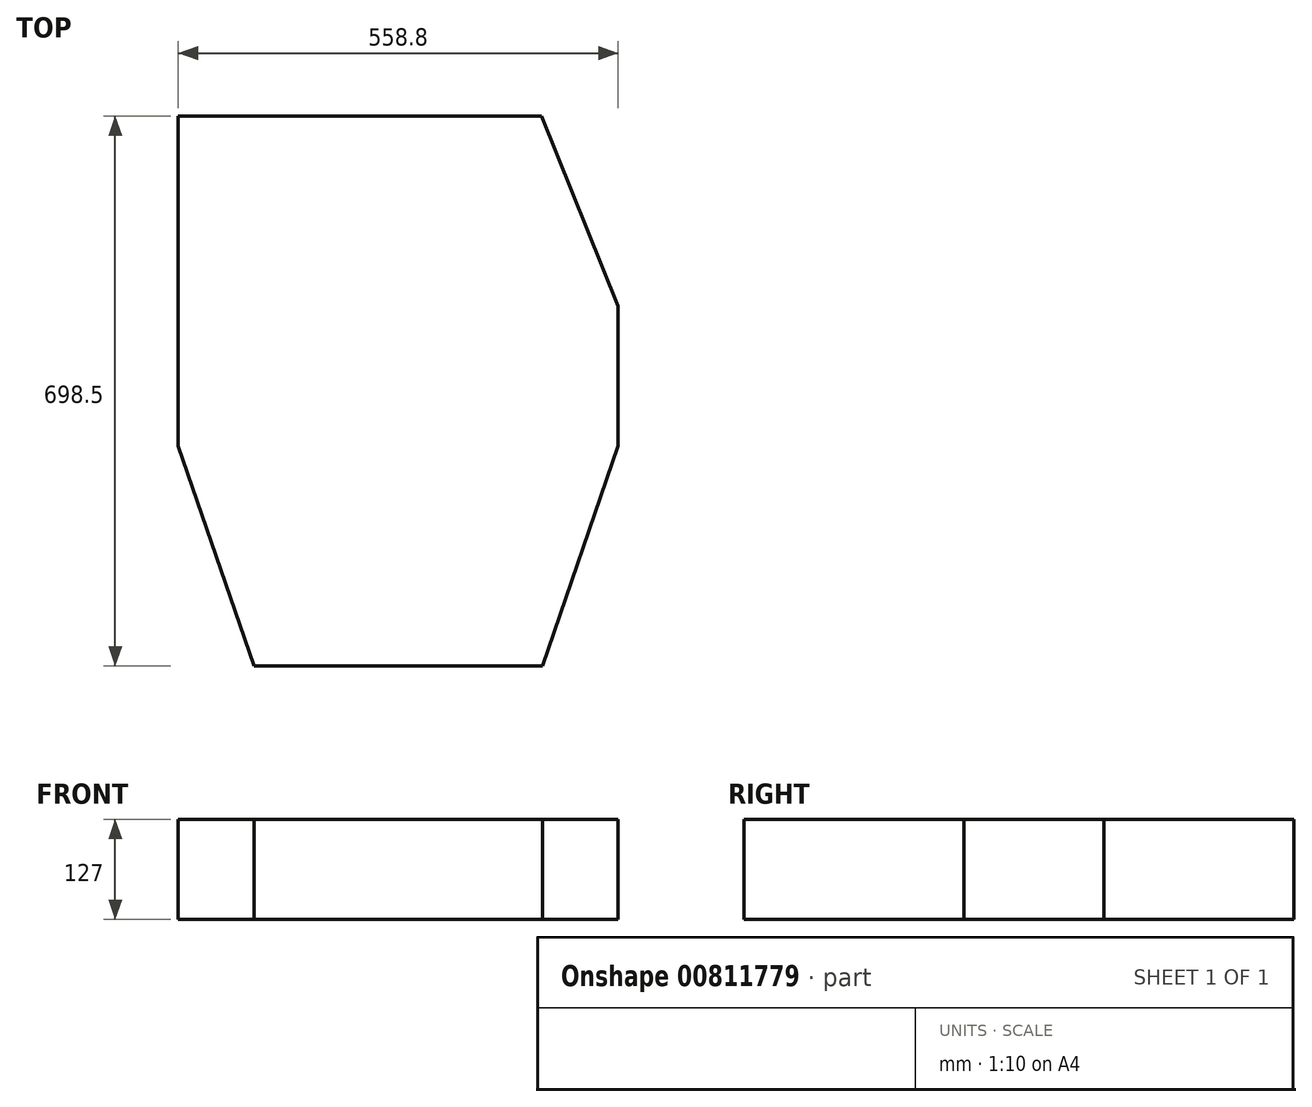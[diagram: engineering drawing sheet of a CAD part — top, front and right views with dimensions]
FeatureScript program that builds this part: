
annotation { "Feature Type Name" : "Feature", "Feature Type Description" : "" }
export const myFeature = defineFeature(function(context is Context, id is Id, definition is map)
    precondition{}
    {
        {
            var Q0;
            Q0=qCreatedBy(makeId("Top.planeOp"),FACE);
            var sketch = newSketch(context, id + "F0", { "sketchPlane" : qUnion([Q0])});
            skLineSegment(sketch, "E0.bottom", {"start": v(279.4, -368.3) * mm, "end": v(-279.4, -368.3) * mm});
            skLineSegment(sketch, "E0.top", {"start": v(279.4, 368.3) * mm, "end": v(-279.4, 368.3) * mm, "construction": true});
            skLineSegment(sketch, "E0.left", {"start": v(279.4, -368.3) * mm, "end": v(279.4, 368.3) * mm});
            skLineSegment(sketch, "E0.right", {"start": v(-279.4, -368.3) * mm, "end": v(-279.4, 368.3) * mm});
            skPoint(sketch, "E0.middle", {"position": v(0, 0) * mm});
            skLineSegment(sketch, "E1.bottom", {"start": v(-279.4, -88.9) * mm, "end": v(-406.4, -88.9) * mm});
            skLineSegment(sketch, "E1.top", {"start": v(-279.4, 88.9) * mm, "end": v(-406.4, 88.9) * mm});
            skLineSegment(sketch, "E1.left", {"start": v(-279.4, -88.9) * mm, "end": v(-279.4, 88.9) * mm});
            skLineSegment(sketch, "E1.right", {"start": v(-406.4, -88.9) * mm, "end": v(-406.4, 88.9) * mm});
            skPoint(sketch, "E1.middle", {"position": v(-342.9, 0) * mm});
            skLineSegment(sketch, "E2.bottom", {"start": v(279.4, 88.9) * mm, "end": v(351.3, 88.9) * mm});
            skLineSegment(sketch, "E2.top", {"start": v(279.4, -88.9) * mm, "end": v(351.3, -88.9) * mm});
            skLineSegment(sketch, "E2.left", {"start": v(279.4, 88.9) * mm, "end": v(279.4, -88.9) * mm});
            skLineSegment(sketch, "E2.right", {"start": v(351.3, 88.9) * mm, "end": v(351.3, -88.9) * mm});
            skPoint(sketch, "E2.middle", {"position": v(315.35, 0) * mm});
            skLineSegment(sketch, "E3", {"start": v(-279.4, 330.2) * mm, "end": v(279.4, 330.2) * mm});
            skLineSegment(sketch, "E4.bottom", {"start": v(-165.1, 304.8) * mm, "end": v(165.1, 304.8) * mm, "construction": true});
            skLineSegment(sketch, "E4.top", {"start": v(-165.1, -25.4) * mm, "end": v(165.1, -25.4) * mm, "construction": true});
            skLineSegment(sketch, "E4.left", {"start": v(-165.1, 304.8) * mm, "end": v(-165.1, -25.4) * mm, "construction": true});
            skLineSegment(sketch, "E4.right", {"start": v(165.1, 304.8) * mm, "end": v(165.1, -25.4) * mm, "construction": true});
            skLineSegment(sketch, "E5.bottom", {"start": v(-165.1, -12.7) * mm, "end": v(165.1, -12.7) * mm, "construction": true});
            skLineSegment(sketch, "E5.top", {"start": v(-165.1, -342.9) * mm, "end": v(165.1, -342.9) * mm, "construction": true});
            skLineSegment(sketch, "E5.left", {"start": v(-165.1, -12.7) * mm, "end": v(-165.1, -342.9) * mm, "construction": true});
            skLineSegment(sketch, "E5.right", {"start": v(165.1, -12.7) * mm, "end": v(165.1, -342.9) * mm, "construction": true});
            skLineSegment(sketch, "E6", {"start": v(-279.4, -88.9) * mm, "end": v(-183.22, -368.3) * mm});
            skLineSegment(sketch, "E7", {"start": v(-279.4, -10.86) * mm, "end": v(-156.36, -368.3) * mm, "construction": true});
            skLineSegment(sketch, "E8", {"start": v(-279.4, 88.9) * mm, "end": v(279.4, 88.9) * mm, "construction": true});
            skLineSegment(sketch, "E9", {"start": v(-279.4, -88.9) * mm, "end": v(279.4, -88.9) * mm, "construction": true});
            skLineSegment(sketch, "E10", {"start": v(279.4, 20.89) * mm, "end": v(165.1, 304.8) * mm, "construction": true});
            skLineSegment(sketch, "E11", {"start": v(279.4, 88.9) * mm, "end": v(182.26, 330.2) * mm});
            skLineSegment(sketch, "E12", {"start": v(0, 0) * mm, "end": v(0, -342.9) * mm, "construction": true});
            skLineSegment(sketch, "E13.MirrorCS", {"start": v(279.4, -88.9) * mm, "end": v(183.22, -368.3) * mm});
            skSolve(sketch);
        }
        {
            var Q0;
            {var subQ0=sQuery(id+"F0.wireOp",EDGE,"E6");Q0=makeQuery(id+"F0.imprint","IMPRINT",FACE,{"disambiguationData":[TD([[makeQuery(id+"F0.imprint","IMPRINT",EDGE,{"derivedFrom":subQ0}),1.0]])]});}
            extrude(context, id + "F1", {"entities" : qUnion([Q0]), "depth" : 127 * mm, "offsetDistance" : 25.4 * mm});
        }
        {
            var Q0;
            Q0=qCreatedBy(makeId("Top.planeOp"),FACE);
            cPlane(context, id + "F2", {"entities" : qUnion([Q0]), "cplaneType" : CPlaneType.OFFSET, "offset" : 508 * mm, "width" : 152.4 * mm, "height" : 152.4 * mm});
        }
        {
            var Q0;
            Q0=qCreatedBy(id+"F2.planeOp",FACE);
            var sketch = newSketch(context, id + "F3", { "sketchPlane" : qUnion([Q0])});
            skLineSegment(sketch, "E14.0", {"start": v(-279.4, 88.9) * mm, "end": v(279.4, 88.9) * mm});
            skLineSegment(sketch, "E14.1", {"start": v(-279.4, -88.9) * mm, "end": v(279.4, -88.9) * mm});
            skLineSegment(sketch, "E14.2", {"start": v(-279.4, -88.9) * mm, "end": v(-279.4, 88.9) * mm});
            skLineSegment(sketch, "E14.3", {"start": v(279.4, 88.9) * mm, "end": v(279.4, -88.9) * mm});
            skSolve(sketch);
        }
        {
            var Q0;
            Q0=makeQuery(id+"F1.opExtrude","CAP_EDGE",EDGE,{"disambiguationData":[OSD([sQuery(id+"F0.wireOp",EDGE,"E0.bottom")])],"isStart":false});
            var Q1;
            Q1=sQuery(id+"F3.wireOp",EDGE,"E14.1");
            loft(context, id + "F4", {"bodyType" : ToolBodyType.SURFACE, "wireProfilesArray" : [{ "wireProfileEntities" : qUnion([Q0]) }, { "wireProfileEntities" : qUnion([Q1]) }]});
        }
        {
            var Q0;
            Q0=makeQuery(id+"F1.opExtrude","CAP_EDGE",EDGE,{"disambiguationData":[OSD([sQuery(id+"F0.wireOp",EDGE,"E13.MirrorCS")])],"isStart":false});
            var Q1;
            Q1=sQuery(id+"F3.wireOp",VERTEX,"E14.1.end");
            loft(context, id + "F5", {"bodyType" : ToolBodyType.SURFACE, "wireProfilesArray" : [{ "wireProfileEntities" : qUnion([Q0]) }, { "wireProfileEntities" : qUnion([Q1]) }]});
        }
        {
            var Q0;
            Q0=sQuery(id+"F3.wireOp",EDGE,"E14.3");
            var Q1;
            Q1=makeQuery(id+"F1.opExtrude","CAP_EDGE",EDGE,{"disambiguationData":[OSD([sQuery(id+"F0.wireOp",EDGE,"E0.left")])],"isStart":false});
            loft(context, id + "F6", {"bodyType" : ToolBodyType.SURFACE, "wireProfilesArray" : [{ "wireProfileEntities" : qUnion([Q0]) }, { "wireProfileEntities" : qUnion([Q1]) }]});
        }
        {
            var Q0;
            Q0=sQuery(id+"F3.wireOp",VERTEX,"E14.0.end");
            var Q1;
            Q1=makeQuery(id+"F1.opExtrude","CAP_EDGE",EDGE,{"disambiguationData":[OSD([sQuery(id+"F0.wireOp",EDGE,"E11")])],"isStart":false});
            loft(context, id + "F7", {"bodyType" : ToolBodyType.SURFACE, "wireProfilesArray" : [{ "wireProfileEntities" : qUnion([Q0]) }, { "wireProfileEntities" : qUnion([Q1]) }]});
        }
        {
            var Q0;
            Q0=sQuery(id+"F3.wireOp",EDGE,"E14.0");
            var Q1;
            Q1=makeQuery(id+"F1.opExtrude","CAP_EDGE",EDGE,{"disambiguationData":[OSD([sQuery(id+"F0.wireOp",EDGE,"E3")])],"isStart":false});
            loft(context, id + "F8", {"bodyType" : ToolBodyType.SURFACE, "wireProfilesArray" : [{ "wireProfileEntities" : qUnion([Q0]) }, { "wireProfileEntities" : qUnion([Q1]) }]});
        }
        {
            var Q0;
            Q0=makeQuery(id+"F1.opExtrude","CAP_EDGE",EDGE,{"disambiguationData":[OSD([sQuery(id+"F0.wireOp",EDGE,"E6")])],"isStart":false});
            var Q1;
            Q1=sQuery(id+"F3.wireOp",VERTEX,"E14.1.start");
            loft(context, id + "F9", {"bodyType" : ToolBodyType.SURFACE, "wireProfilesArray" : [{ "wireProfileEntities" : qUnion([Q0]) }, { "wireProfileEntities" : qUnion([Q1]) }]});
        }
        {
            var Q0;
            Q0=makeQuery(id+"F1.opExtrude","CAP_EDGE",EDGE,{"disambiguationData":[OSD([sQuery(id+"F0.wireOp",EDGE,"E0.right")])],"isStart":false});
            var Q1;
            Q1=sQuery(id+"F3.wireOp",EDGE,"E14.2");
            loft(context, id + "F10", {"bodyType" : ToolBodyType.SURFACE, "wireProfilesArray" : [{ "wireProfileEntities" : qUnion([Q0]) }, { "wireProfileEntities" : qUnion([Q1]) }]});
        }
        {
            var Q0;
            Q0=sQuery(id+"F3.wireOp",EDGE,"E14.3");
            var Q1;
            Q1=sQuery(id+"F3.wireOp",EDGE,"E14.2");
            loft(context, id + "F11", {"bodyType" : ToolBodyType.SURFACE, "surfaceOperationType" : NewSurfaceOperationType.ADD, "wireProfilesArray" : [{ "wireProfileEntities" : qUnion([Q0]) }, { "wireProfileEntities" : qUnion([Q1]) }]});
        }
    });
